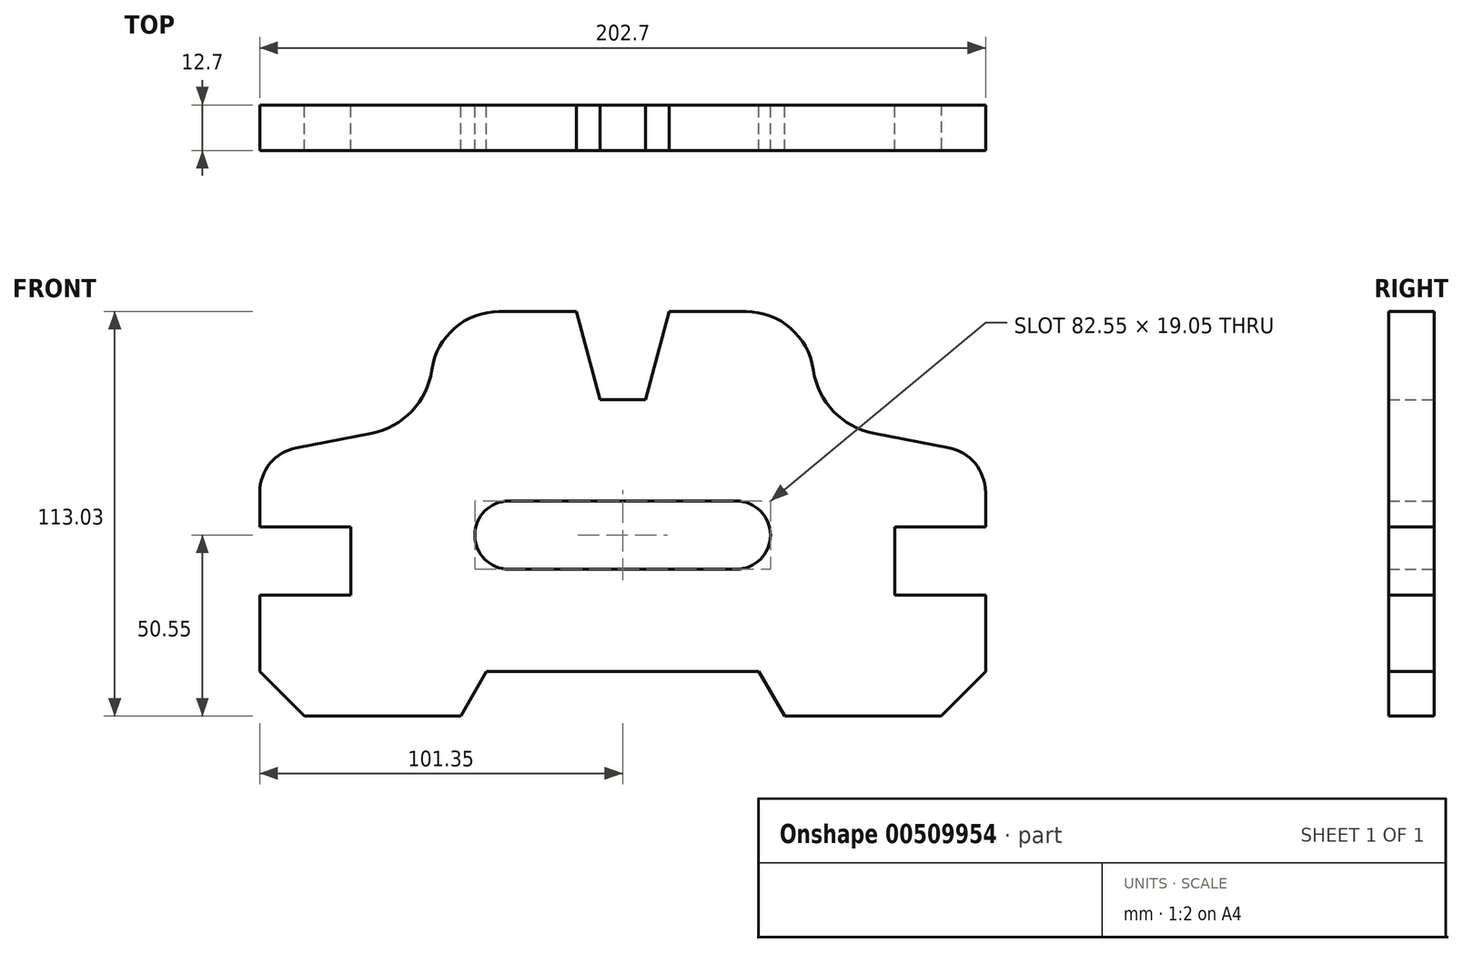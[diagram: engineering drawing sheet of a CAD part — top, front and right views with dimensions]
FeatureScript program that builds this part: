
annotation { "Feature Type Name" : "Feature", "Feature Type Description" : "" }
export const myFeature = defineFeature(function(context is Context, id is Id, definition is map)
    precondition{}
    {
        {
            var Q0;
            Q0=qCreatedBy(makeId("Front.planeOp"),FACE);
            var sketch = newSketch(context, id + "F0", { "sketchPlane" : qUnion([Q0])});
            skLineSegment(sketch, "E0.bottom", {"start": v(31.75, 9.53) * mm, "end": v(-31.75, 9.53) * mm});
            skLineSegment(sketch, "E0.top", {"start": v(31.75, -9.52) * mm, "end": v(-31.75, -9.52) * mm});
            skPoint(sketch, "E0.middle", {"position": v(0, 0) * mm});
            skArc(sketch, "E1", {"start": v(31.75, -9.53) * mm, "mid": v(41.27, 0) * mm, "end": v(31.75, 9.53) * mm});
            skArc(sketch, "E2", {"start": v(-31.75, 9.53) * mm, "mid": v(-41.28, 0) * mm, "end": v(-31.75, -9.53) * mm});
            skLineSegment(sketch, "E3", {"start": v(0, 75.38) * mm, "end": v(0, -75.34) * mm, "construction": true});
            skLineSegment(sketch, "E4", {"start": v(0, 37.85) * mm, "end": v(6.35, 37.85) * mm});
            skLineSegment(sketch, "E5", {"start": v(6.35, 37.85) * mm, "end": v(12.95, 62.48) * mm});
            skLineSegment(sketch, "E6", {"start": v(12.95, 62.48) * mm, "end": v(34.43, 62.48) * mm});
            skArc(sketch, "E7", {"start": v(34.43, 62.48) * mm, "mid": v(46.9, 57.83) * mm, "end": v(53.28, 46.13) * mm});
            skArc(sketch, "E8", {"start": v(53.28, 46.13) * mm, "mid": v(58.87, 34.61) * mm, "end": v(70.1, 28.46) * mm});
            skLineSegment(sketch, "E9", {"start": v(70.1, 28.46) * mm, "end": v(91.06, 24.4) * mm});
            skArc(sketch, "E10", {"start": v(91.06, 24.4) * mm, "mid": v(98.44, 20.02) * mm, "end": v(101.35, 11.94) * mm});
            skLineSegment(sketch, "E11", {"start": v(101.35, 11.94) * mm, "end": v(101.35, 2.29) * mm});
            skLineSegment(sketch, "E12", {"start": v(101.35, 2.29) * mm, "end": v(75.95, 2.29) * mm});
            skLineSegment(sketch, "E13", {"start": v(75.95, 2.29) * mm, "end": v(75.95, -16.76) * mm});
            skLineSegment(sketch, "E14", {"start": v(75.95, -16.76) * mm, "end": v(101.35, -16.76) * mm});
            skLineSegment(sketch, "E15", {"start": v(101.35, -16.76) * mm, "end": v(101.35, -50.55) * mm});
            skLineSegment(sketch, "E16", {"start": v(101.35, -50.55) * mm, "end": v(45.21, -50.55) * mm});
            skLineSegment(sketch, "E17", {"start": v(45.21, -50.55) * mm, "end": v(38.03, -38.1) * mm});
            skLineSegment(sketch, "E18", {"start": v(38.03, -38.1) * mm, "end": v(0, -38.1) * mm});
            skLineSegment(sketch, "E19", {"start": v(6.35, 37.85) * mm, "end": v(6.35, 71.29) * mm, "construction": true});
            skLineSegment(sketch, "E20.MirrorCS", {"start": v(0, 37.85) * mm, "end": v(-6.35, 37.85) * mm});
            skLineSegment(sketch, "E21.MirrorCS", {"start": v(-6.35, 37.85) * mm, "end": v(-12.95, 62.48) * mm});
            skLineSegment(sketch, "E22.MirrorCS", {"start": v(-12.95, 62.48) * mm, "end": v(-34.43, 62.48) * mm});
            skArc(sketch, "E23.MirrorCS", {"start": v(-34.43, 62.48) * mm, "mid": v(-46.9, 57.83) * mm, "end": v(-53.28, 46.13) * mm});
            skArc(sketch, "E24.MirrorCS", {"start": v(-53.28, 46.13) * mm, "mid": v(-58.87, 34.61) * mm, "end": v(-70.1, 28.46) * mm});
            skLineSegment(sketch, "E25.MirrorCS", {"start": v(-70.1, 28.46) * mm, "end": v(-91.06, 24.4) * mm});
            skArc(sketch, "E26.MirrorCS", {"start": v(-91.06, 24.4) * mm, "mid": v(-98.44, 20.02) * mm, "end": v(-101.35, 11.94) * mm});
            skLineSegment(sketch, "E27.MirrorCS", {"start": v(-101.35, 11.94) * mm, "end": v(-101.35, 2.29) * mm});
            skLineSegment(sketch, "E28.MirrorCS", {"start": v(-101.35, 2.29) * mm, "end": v(-75.95, 2.29) * mm});
            skLineSegment(sketch, "E29.MirrorCS", {"start": v(-75.95, 2.29) * mm, "end": v(-75.95, -16.76) * mm});
            skLineSegment(sketch, "E30.MirrorCS", {"start": v(-75.95, -16.76) * mm, "end": v(-101.35, -16.76) * mm});
            skLineSegment(sketch, "E31.MirrorCS", {"start": v(-101.35, -16.76) * mm, "end": v(-101.35, -50.55) * mm});
            skLineSegment(sketch, "E32.MirrorCS", {"start": v(-101.35, -50.55) * mm, "end": v(-45.21, -50.55) * mm});
            skLineSegment(sketch, "E33.MirrorCS", {"start": v(-45.21, -50.55) * mm, "end": v(-38.03, -38.1) * mm});
            skLineSegment(sketch, "E34.MirrorCS", {"start": v(-38.03, -38.1) * mm, "end": v(0, -38.1) * mm});
            skLineSegment(sketch, "E35", {"start": v(-6.35, 37.85) * mm, "end": v(-6.35, 70.69) * mm, "construction": true});
            skLineSegment(sketch, "E36", {"start": v(38.03, -38.1) * mm, "end": v(38.03, -55.68) * mm, "construction": true});
            skSolve(sketch);
        }
        {
            var Q0;
            Q0 = qSketchRegion(id + "F0", true);
            extrude(context, id + "F1", {"entities" : qUnion([Q0]), "endBound" : BoundingType.SYMMETRIC, "depth" : 12.7 * mm, "offsetDistance" : 25.4 * mm});
        }
        {
            var Q0;
            Q0=makeQuery(id+"F1.opExtrude","SWEPT_EDGE",EDGE,{"disambiguationData":[OSD([sQuery(id+"F0.wireOp",EDGE,"E31.MirrorCS"),sQuery(id+"F0.wireOp",EDGE,"E32.MirrorCS")])]});
            var Q1;
            Q1=makeQuery(id+"F1.opExtrude","SWEPT_EDGE",EDGE,{"disambiguationData":[OSD([sQuery(id+"F0.wireOp",EDGE,"E15"),sQuery(id+"F0.wireOp",EDGE,"E16")])]});
            chamfer(context, id + "F2", {"entities" : qUnion([Q0, Q1]), "width" : 12.45 * mm, "tangentPropagation" : true});
        }
    });
